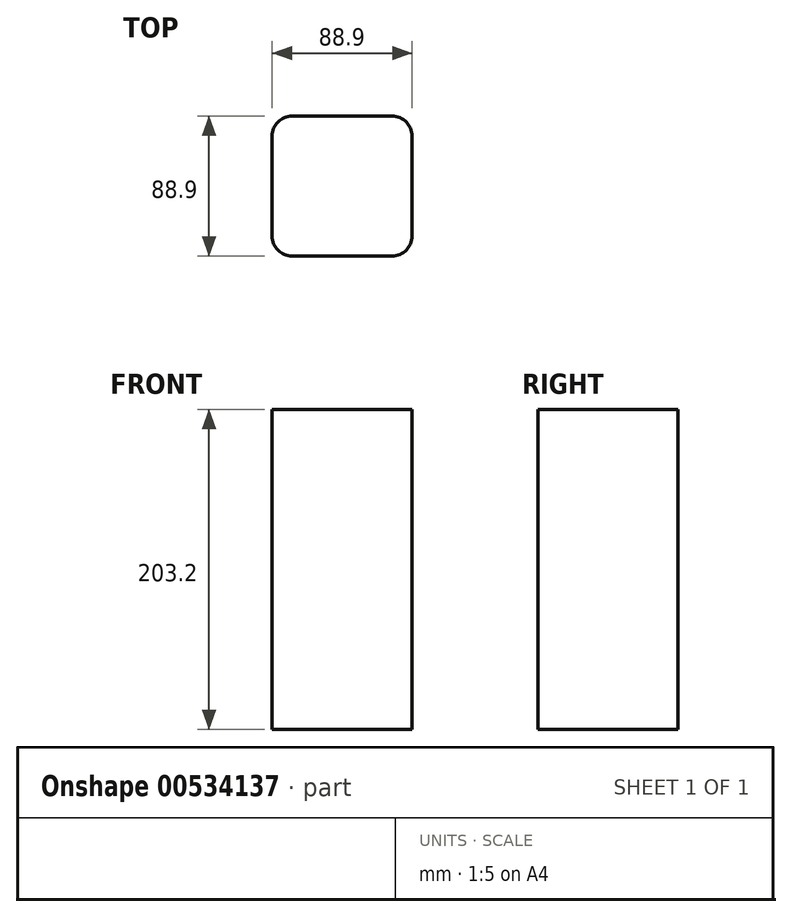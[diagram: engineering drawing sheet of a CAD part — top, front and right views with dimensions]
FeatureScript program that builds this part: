
annotation { "Feature Type Name" : "Feature", "Feature Type Description" : "" }
export const myFeature = defineFeature(function(context is Context, id is Id, definition is map)
    precondition{}
    {
        {
            var Q0;
            Q0=qCreatedBy(makeId("Top.planeOp"),FACE);
            var sketch = newSketch(context, id + "F0", { "sketchPlane" : qUnion([Q0])});
            skLineSegment(sketch, "E0.bottom", {"start": v(-44.45, 44.45) * mm, "end": v(44.45, 44.45) * mm});
            skLineSegment(sketch, "E0.top", {"start": v(-44.45, -44.45) * mm, "end": v(44.45, -44.45) * mm});
            skLineSegment(sketch, "E0.left", {"start": v(-44.45, 44.45) * mm, "end": v(-44.45, -44.45) * mm});
            skLineSegment(sketch, "E0.right", {"start": v(44.45, 44.45) * mm, "end": v(44.45, -44.45) * mm});
            skSolve(sketch);
        }
        {
            var Q0;
            Q0=makeQuery(id+"F0.imprint","IMPRINT",FACE,{"disambiguationData":[TD([[makeQuery(id+"F0.imprint","IMPRINT",EDGE,{"derivedFrom":sQuery(id+"F0.wireOp",EDGE,"E0.bottom")}),-1.0]])]});
            extrude(context, id + "F1", {"entities" : qUnion([Q0]), "depth" : 203.2 * mm, "offsetDistance" : 25.4 * mm});
        }
        {
            var Q0;
            Q0=makeQuery(id+"F1.opExtrude","SWEPT_EDGE",EDGE,{"disambiguationData":[OSD([sQuery(id+"F0.wireOp",EDGE,"E0.top"),sQuery(id+"F0.wireOp",EDGE,"E0.right")])]});
            var Q1;
            Q1=makeQuery(id+"F1.opExtrude","SWEPT_EDGE",EDGE,{"disambiguationData":[OSD([sQuery(id+"F0.wireOp",EDGE,"E0.bottom"),sQuery(id+"F0.wireOp",EDGE,"E0.right")])]});
            var Q2;
            Q2=makeQuery(id+"F1.opExtrude","SWEPT_EDGE",EDGE,{"disambiguationData":[OSD([sQuery(id+"F0.wireOp",EDGE,"E0.top"),sQuery(id+"F0.wireOp",EDGE,"E0.left")])]});
            var Q3;
            Q3=makeQuery(id+"F1.opExtrude","SWEPT_EDGE",EDGE,{"disambiguationData":[OSD([sQuery(id+"F0.wireOp",EDGE,"E0.bottom"),sQuery(id+"F0.wireOp",EDGE,"E0.left")])]});
            fillet(context, id + "F2", {"entities" : qUnion([Q0, Q1, Q2, Q3]), "radius" : 12.7 * mm, "tangentPropagation" : true, "allowEdgeOverflow" : false});
        }
    });
